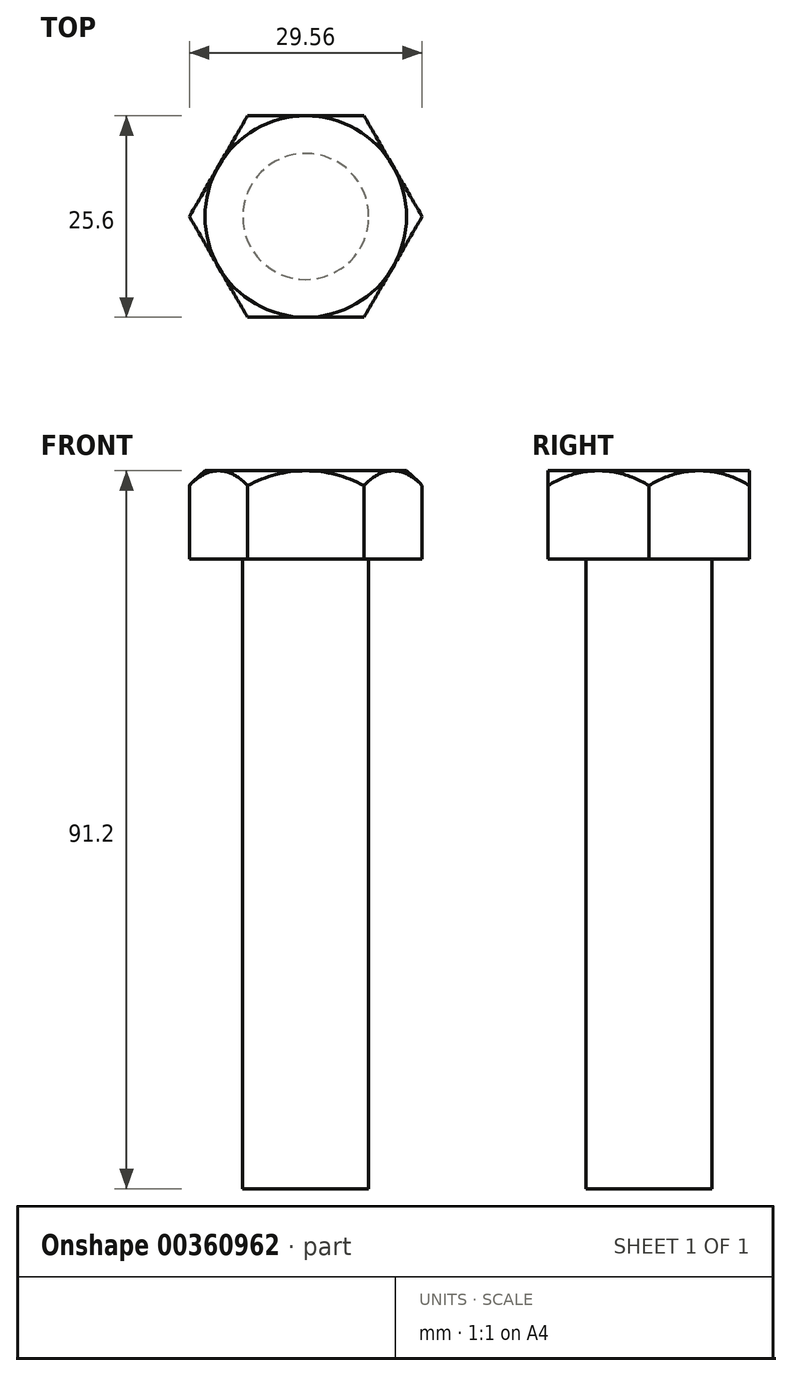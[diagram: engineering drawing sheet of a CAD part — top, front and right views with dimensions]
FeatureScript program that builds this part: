
annotation { "Feature Type Name" : "Feature", "Feature Type Description" : "" }
export const myFeature = defineFeature(function(context is Context, id is Id, definition is map)
    precondition{}
    {
        {
            assignVariable(context, id + "F0", {"name" : "D", "anyValue" : 16});
        }
        {
            var Q0;
            Q0=qCreatedBy(makeId("Top.planeOp"),FACE);
            var sketch = newSketch(context, id + "F1", { "sketchPlane" : qUnion([Q0])});
            skCircle(sketch, "E0.cCircle", {"center": v(0, 0) * mm, "radius": 12.8 * mm, "construction": true});
            skLineSegment(sketch, "E0.0", {"start": v(-7.4, 12.8) * mm, "end": v(7.4, 12.8) * mm});
            skLineSegment(sketch, "E0.1", {"start": v(7.4, 12.8) * mm, "end": v(14.78, 0) * mm});
            skLineSegment(sketch, "E0.2", {"start": v(14.78, 0) * mm, "end": v(7.4, -12.8) * mm});
            skLineSegment(sketch, "E0.3", {"start": v(7.4, -12.8) * mm, "end": v(-7.4, -12.8) * mm});
            skLineSegment(sketch, "E0.4", {"start": v(-7.4, -12.8) * mm, "end": v(-14.78, 0) * mm});
            skLineSegment(sketch, "E0.5", {"start": v(-14.78, 0) * mm, "end": v(-7.4, 12.8) * mm});
            skPoint(sketch, "E0.0.midPoint", {"position": v(0, 12.8) * mm});
            skSolve(sketch);
        }
        {
            var Q0;
            Q0=makeQuery(id+"F1.imprint","IMPRINT",FACE,{"disambiguationData":[TD([[makeQuery(id+"F1.imprint","IMPRINT",EDGE,{"derivedFrom":sQuery(id+"F1.wireOp",EDGE,"E0.0")}),-1.0]])]});
            extrude(context, id + "F2", {"entities" : qUnion([Q0]), "depth" : (0.7 * getVariable(context, 'D')) * mm, "offsetDistance" : 25 * mm});
        }
        {
            var Q0;
            Q0=qCreatedBy(makeId("Top.planeOp"),FACE);
            var sketch = newSketch(context, id + "F3", { "sketchPlane" : qUnion([Q0])});
            skCircle(sketch, "E1", {"center": v(0, 0) * mm, "radius": 8 * mm});
            skSolve(sketch);
        }
        {
            var Q0;
            Q0=makeQuery(id+"F3.imprint","IMPRINT",FACE,{"disambiguationData":[TD([[makeQuery(id+"F3.imprint","IMPRINT",EDGE,{"derivedFrom":sQuery(id+"F3.wireOp",EDGE,"E1")}),1.0]])]});
            extrude(context, id + "F4", {"entities" : qUnion([Q0]), "operationType" : NewBodyOperationType.ADD, "oppositeDirection" : true, "depth" : 80 * mm, "offsetDistance" : 25 * mm});
        }
        {
            var Q0;
            Q0=qCreatedBy(makeId("Right.planeOp"),FACE);
            var sketch = newSketch(context, id + "F5", { "sketchPlane" : qUnion([Q0])});
            skLineSegment(sketch, "E2", {"start": v(30, 20) * mm, "end": v(0, 20) * mm});
            skLineSegment(sketch, "E3", {"start": v(30, 20) * mm, "end": v(30, 0) * mm});
            skLineSegment(sketch, "E4", {"start": v(30, 0) * mm, "end": v(19.56, 0) * mm});
            skPoint(sketch, "E5", {"position": v(12.8, 11.2) * mm});
            skArc(sketch, "E6", {"start": v(19.56, 0) * mm, "mid": v(12.58, 11.38) * mm, "end": v(0, 15.83) * mm});
            skLineSegment(sketch, "E7", {"start": v(0, 20) * mm, "end": v(0, 15.83) * mm});
            skSolve(sketch);
        }
        {
            var Q0;
            Q0=makeQuery(id+"F5.imprint","IMPRINT",FACE,{"disambiguationData":[TD([[makeQuery(id+"F5.imprint","IMPRINT",EDGE,{"derivedFrom":sQuery(id+"F5.wireOp",EDGE,"E2")}),1.0]])]});
            var Q1;
            Q1=sQuery(id+"F5.wireOp",EDGE,"E7");
            revolve(context, id + "F6", {"operationType" : NewBodyOperationType.REMOVE, "entities" : qUnion([Q0]), "axis" : qUnion([Q1]), "revolveType" : RevolveType.FULL, "oppositeDirection" : true});
        }
    });
